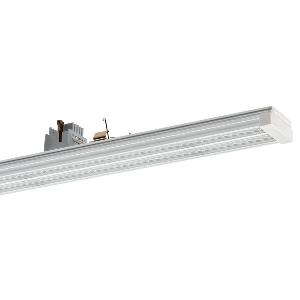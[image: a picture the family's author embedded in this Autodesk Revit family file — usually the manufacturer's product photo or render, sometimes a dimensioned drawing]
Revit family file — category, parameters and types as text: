
# Revit family: conveo_-_cvg_15000_850_w-l_ea_5_226848369-00804975_d492
name_source: partatom
category: Lighting Fixtures
units: mm (PartAtom-declared; Revit-internal decimal feet)

## family parameters
Cut with Voids When Loaded = No
Host = Face
Light Source = No
Part Type = Normal
Room Calculation Point = No
Round Connector Dimension = Use Diameter
Shared = No

## types (1)
- CONVEO - CVG 15000/850/W-L/EA/5 (1 x LED, 14800 lm, 5000K)
    Apparent Load = 86 VA
    Approval mark = CE
    CIE Flux Codes = 85 97 99 100 100
    Color Rendering = 80-89
    Color Temperature = 5000K
    Control Gear = Electronic ballast
    Default Elevation = 1800 mm
    Description = CVG 15000/850/W-L/EA/5|Continuous-row system|light source: LED|work equipment: Electronic ballast|connected load: 220-240 V, 50-60 Hz|Power consumption: approx. 86 W|luminous flux: 14800 lm|luminous efficacy: 172 lm/W|colour temperature: Cold white, ca. 5000 K|color rendering index (CRI): >= 80|chromaticity tolerance:  3 SDCM|System of protection: IP 54|class of protection: I|technology: Switchable|luminaire body|material: Aluminium|surface: Powder coatet|colour: White|lamp cover: Acrylic (PMMA), Satine|weight (net): approx. 2.2 kg|Fastening: Available separately|maximum ambient temperature: 41 ░C|glare control: Lens optics|Approval mark: VDE - ENEC|
    Frequency = 50 Hz
    Height = 70 mm
    Lamp = 1 x LED
    Lamp Light Flux = 14800 lm
    Lamp count = 1
    Length = 1500 mm
    Luminous efficacy = 172 lm/W
    Manufacturer = Waldmann
    ModVariant = No
    Model = 226848369-00804975
    Mounting Place = Ceiling
    Mounting Type = Pendant
    Number of Poles = 1
    OnlyDefault = Yes
    Power Factor = 1
    Product Name = CONVEO - CVG 15000/850/W-L/EA/5
    Product group = Continuous-row system (industry)
    ProductGroupID = 301
    Protection Class = Protection class I
    Protection Degree = IP 54
    RLX_Detail_Level = 1
    RlxData = <blob elided: 135677 chars, md5=be2e0f00>
    Socket = socket
    Standby Power = 0 W
    System Light Flux = 14800 lm
    System Power = 86 W
    Type Comments = Product without accessories
    Type Image = 226848359-00804974-2l5.jpg
    URL = http://relux.com
    VarID = ---
    Voltage = 230 V
    Voltage Range = 220-240 V
    Weight = 0.00 kg
    Width = 64 mm

## geometry (parser evidence)
native form markers: Blend x4, Sweep x12
no freeform markers — native parametric forms only
